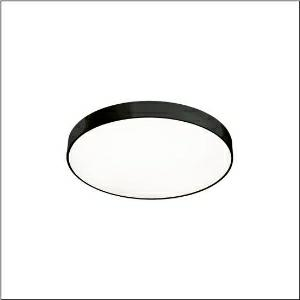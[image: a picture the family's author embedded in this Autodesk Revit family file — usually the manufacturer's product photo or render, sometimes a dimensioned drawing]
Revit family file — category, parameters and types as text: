
# Revit family: round_21_m_51mr36gd0421b
name_source: partatom
category: Lighting Fixtures
units: mm (PartAtom-declared; Revit-internal decimal feet)

## family parameters
Cut with Voids When Loaded = No
Host = Face
Light Source = No
Part Type = Normal
Room Calculation Point = No
Round Connector Dimension = Use Diameter
Shared = No

## types (1)
- Round 21 M (1 x LED, 7870 lm, 54.6 W, 4000K)
    Apparent Load = 55 VA
    CIE Flux Codes = 49 80 96 85 100
    Color Rendering = 80
    Color Temperature = 4000K
    Default Elevation = 1800 mm
    Description = Round 21 M, wall and ceiling luminaire, primary optical cover: cover, of PMMA, opal, light emission: direct/indirect distribution, primary light characteristic: symmetric, installation type: suspended mounting, surface-mounted, LED, rated luminous flux: 7.870lm, luminous efficacy: 144lm/W, light colour: 840, colour temperature: 4000K, control gear: DALI 2, with terminal, 5-pole, mains connection: 230V, AC, 50/60Hz, rated input power: 54.6W, housing, of aluminium, coated, black, diameter: 600mm, height: 62mm, protection rating (complete): IP40, insulation class (complete): insulation class I (protective earthing), certification: CE, impact resistance: IK04, permissible operating ambient temperature: -10..+35°C, packaging unit: 1 piece
    Height = 87 mm
    Lamp = 1 x LED
    Lamp Light Flux = 7870 lm
    Lamp Power = 54.6 W
    Lamp count = 1
    Length = 600 mm
    Luminous efficacy = 144 lm/W
    Manufacturer = Siteco
    ModVariant = No
    Model = 51MR36GD0421B
    Mounting Place = Ceiling
    Mounting Type = Surface mounted
    Number of Poles = 1
    OnlyDefault = Yes
    Power Factor = 1
    Product Name = Round 21 M
    Product group = wall and ceiling luminaire | ceiling mounted
    ProductGroupID = 304
    Protection Class = Protection class I
    Protection Degree = IP 40
    RLX_Detail_Level = 1
    RLX_Emergency_Light_Flux = 0 lm
    RLX_Emergency_Type = 0
    RLX_Emergency_Type_DB = No
    RlxData = <blob elided: 18157 chars, md5=fc33265d>
    Socket = socket
    Standby Power = 0 W
    System Light Flux = 7870 lm
    System Power = 55 W
    Type Comments = Product without accessories
    Type Image = l_1258332.jpg
    URL = http://relux.com
    VarID = ---
    Voltage = 0 V
    Weight = 0.00 kg
    Width = 0 mm  [stored 0 ft]

note: [stored X ft] marks values corroborated as IEEE doubles in the binary element streams (Revit-internal decimal feet)

## geometry (parser evidence)
native form markers: Blend x4, Sweep x11
no freeform markers — native parametric forms only
